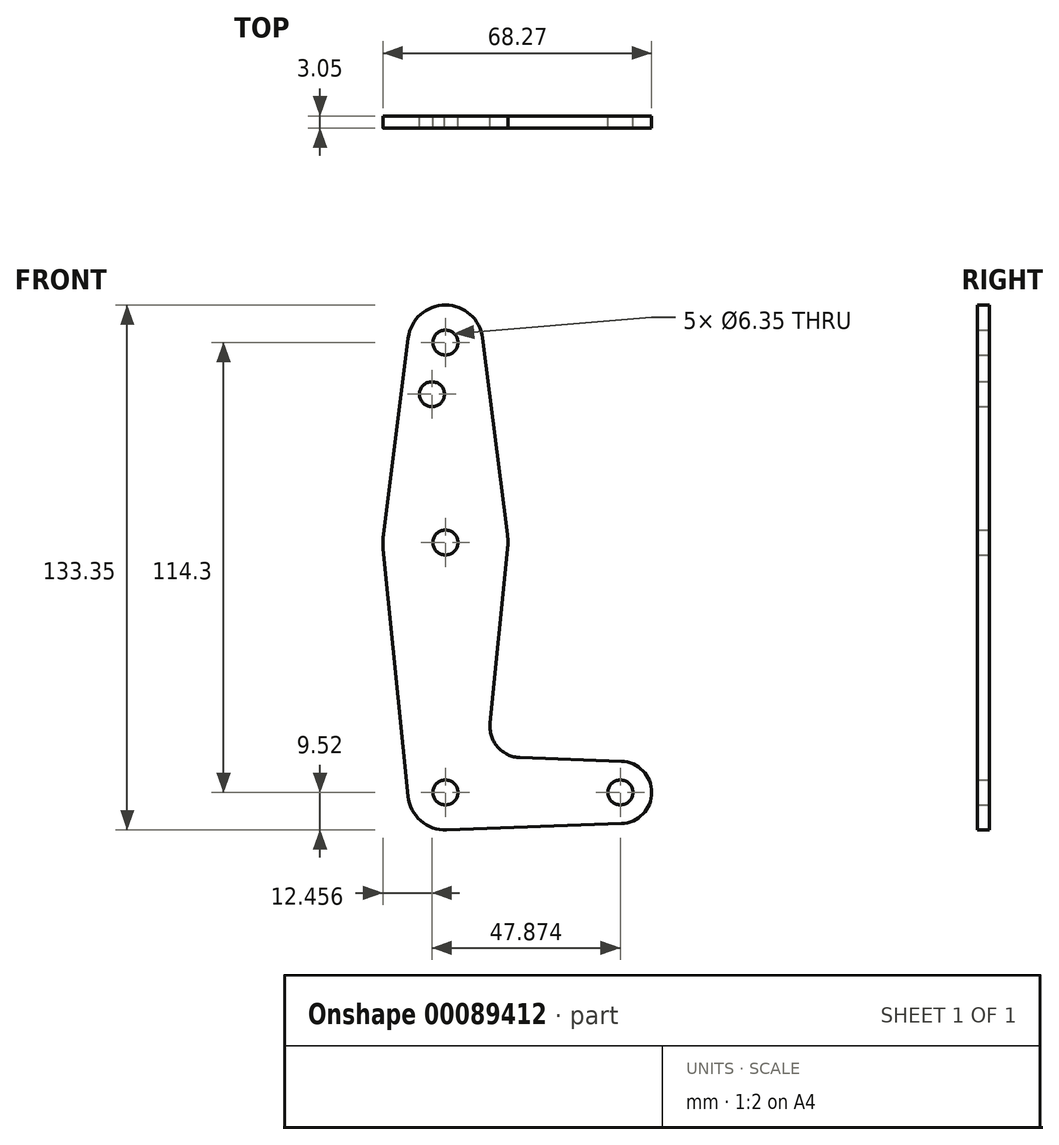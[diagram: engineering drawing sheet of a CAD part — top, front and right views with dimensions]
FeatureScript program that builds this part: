
annotation { "Feature Type Name" : "Feature", "Feature Type Description" : "" }
export const myFeature = defineFeature(function(context is Context, id is Id, definition is map)
    precondition{}
    {
        {
            var Q0;
            Q0=qCreatedBy(makeId("Front.planeOp"),FACE);
            var sketch = newSketch(context, id + "F0", { "sketchPlane" : qUnion([Q0])});
            skLineSegment(sketch, "E0", {"start": v(0, 114.3) * mm, "end": v(0, 0) * mm});
            skLineSegment(sketch, "E1", {"start": v(0, 0) * mm, "end": v(44.45, 0) * mm});
            skCircle(sketch, "E2", {"center": v(0, 114.3) * mm, "radius": 9.52 * mm});
            skCircle(sketch, "E3", {"center": v(0, 63.5) * mm, "radius": 15.88 * mm});
            skCircle(sketch, "E4", {"center": v(0, 0) * mm, "radius": 9.53 * mm});
            skCircle(sketch, "E5", {"center": v(44.45, 0) * mm, "radius": 7.94 * mm});
            skLineSegment(sketch, "E6", {"start": v(-9.45, 115.5) * mm, "end": v(-15.75, 65.48) * mm});
            skLineSegment(sketch, "E7", {"start": v(-15.8, 61.91) * mm, "end": v(-9.48, -0.95) * mm});
            skLineSegment(sketch, "E8", {"start": v(11.34, 17.6) * mm, "end": v(15.8, 61.91) * mm});
            skLineSegment(sketch, "E9", {"start": v(15.75, 65.48) * mm, "end": v(9.45, 115.5) * mm});
            skLineSegment(sketch, "E10", {"start": v(18.97, 8.85) * mm, "end": v(44.73, 7.93) * mm});
            skLineSegment(sketch, "E11", {"start": v(0.34, -9.52) * mm, "end": v(44.73, -7.93) * mm});
            skCircle(sketch, "E12", {"center": v(0, 114.3) * mm, "radius": 3.18 * mm});
            skCircle(sketch, "E13", {"center": v(0, 63.5) * mm, "radius": 3.18 * mm});
            skCircle(sketch, "E14", {"center": v(0, 0) * mm, "radius": 3.18 * mm});
            skCircle(sketch, "E15", {"center": v(44.45, 0) * mm, "radius": 3.18 * mm});
            skCircle(sketch, "E16", {"center": v(-3.42, 101.17) * mm, "radius": 3.18 * mm});
            skPoint(sketch, "E17.newPointA", {"position": v(9.48, -0.95) * mm});
            skArc(sketch, "E17.filletArc", {"start": v(11.34, 17.6) * mm, "mid": v(13.26, 11.57) * mm, "end": v(18.97, 8.85) * mm});
            skSolve(sketch);
        }
        {
            var Q0;
            Q0 = qSketchRegion(id + "F0", true);
            extrude(context, id + "F1", {"entities" : qUnion([Q0]), "depth" : 3.05 * mm});
        }
        {
            var Q0;
            {var subQ0=sQuery(id+"F0.wireOp",EDGE,"E4");var subQ1=sQuery(id+"F0.wireOp",EDGE,"E0");var subQ2=makeQuery(id+"F0.imprint","INTERSECT",VERTEX,{"derivedFrom":[subQ1,subQ0]});Q0=makeQuery(id+"F0.imprint","IMPRINT",FACE,{"disambiguationData":[TD([[makeQuery(id+"F0.imprint","IMPRINT",EDGE,{"disambiguationData":[TD([[subQ2,-1.0]])],"derivedFrom":subQ1}),1.0]])]});}
            extrude(context, id + "F2", {"entities" : qUnion([Q0]), "operationType" : NewBodyOperationType.ADD, "depth" : 3.05 * mm});
        }
    });
